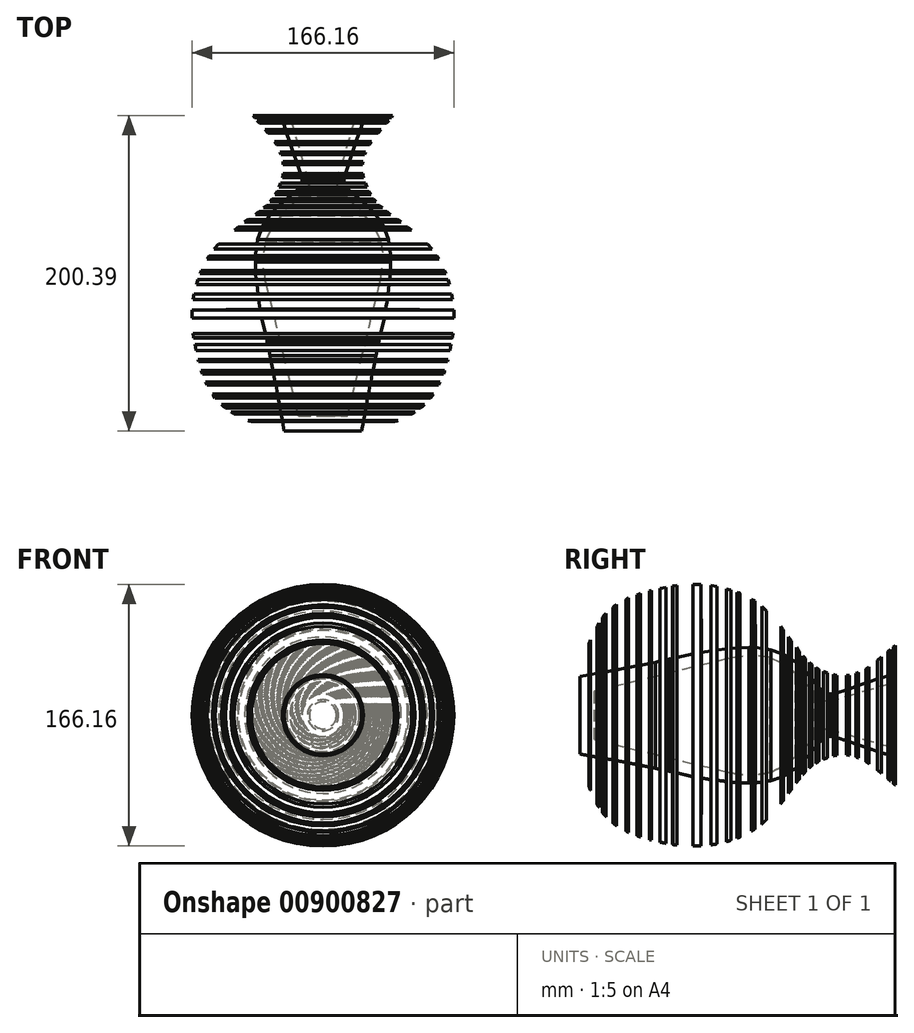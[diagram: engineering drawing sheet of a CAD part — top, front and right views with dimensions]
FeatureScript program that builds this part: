
annotation { "Feature Type Name" : "Feature", "Feature Type Description" : "" }
export const myFeature = defineFeature(function(context is Context, id is Id, definition is map)
    precondition{}
    {
        {
            var Q0;
            Q0=qCreatedBy(makeId("Top.planeOp"),FACE);
            var sketch = newSketch(context, id + "F0", { "sketchPlane" : qUnion([Q0])});
            skLineSegment(sketch, "E0", {"start": v(0, 0) * mm, "end": v(24.6, 0) * mm});
            skLineSegment(sketch, "E1", {"start": v(24.6, 0) * mm, "end": v(25.7, 6) * mm});
            skLineSegment(sketch, "E2", {"start": v(25.7, 6) * mm, "end": v(45.48, 6) * mm});
            skLineSegment(sketch, "E3", {"start": v(45.48, 6) * mm, "end": v(46.94, 6.45) * mm});
            skLineSegment(sketch, "E4", {"start": v(46.94, 6.45) * mm, "end": v(47.72, 6.74) * mm});
            skLineSegment(sketch, "E5", {"start": v(47.72, 6.74) * mm, "end": v(25.83, 6.74) * mm});
            skLineSegment(sketch, "E6", {"start": v(25.83, 6.74) * mm, "end": v(26.57, 10.86) * mm});
            skLineSegment(sketch, "E7", {"start": v(26.57, 10.86) * mm, "end": v(56.36, 10.86) * mm});
            skLineSegment(sketch, "E8", {"start": v(56.36, 10.86) * mm, "end": v(57.49, 11.54) * mm});
            skLineSegment(sketch, "E9", {"start": v(57.49, 11.54) * mm, "end": v(58.5, 12.14) * mm});
            skLineSegment(sketch, "E10", {"start": v(58.5, 12.14) * mm, "end": v(26.8, 12.14) * mm});
            skLineSegment(sketch, "E11", {"start": v(26.8, 12.14) * mm, "end": v(27.05, 13.55) * mm});
            skLineSegment(sketch, "E12", {"start": v(27.05, 13.55) * mm, "end": v(27.23, 14.54) * mm});
            skLineSegment(sketch, "E13", {"start": v(27.23, 14.54) * mm, "end": v(62, 14.54) * mm});
            skLineSegment(sketch, "E14", {"start": v(62, 14.54) * mm, "end": v(63.25, 15.43) * mm});
            skLineSegment(sketch, "E15", {"start": v(63.25, 15.43) * mm, "end": v(64.53, 16.71) * mm});
            skLineSegment(sketch, "E16", {"start": v(64.53, 16.71) * mm, "end": v(27.63, 16.71) * mm});
            skLineSegment(sketch, "E17", {"start": v(27.63, 16.71) * mm, "end": v(28.63, 22.26) * mm});
            skLineSegment(sketch, "E18", {"start": v(28.63, 22.26) * mm, "end": v(28.4, 20.96) * mm});
            skLineSegment(sketch, "E19", {"start": v(28.4, 20.96) * mm, "end": v(68.43, 20.96) * mm});
            skLineSegment(sketch, "E20", {"start": v(68.43, 20.96) * mm, "end": v(69.66, 22.52) * mm});
            skLineSegment(sketch, "E21", {"start": v(69.66, 22.52) * mm, "end": v(70.23, 23.46) * mm});
            skLineSegment(sketch, "E22", {"start": v(70.23, 23.46) * mm, "end": v(28.86, 23.46) * mm});
            skLineSegment(sketch, "E23", {"start": v(28.86, 23.46) * mm, "end": v(29.9, 29.26) * mm});
            skLineSegment(sketch, "E24", {"start": v(29.9, 29.26) * mm, "end": v(73.52, 29.26) * mm});
            skLineSegment(sketch, "E25", {"start": v(73.52, 29.26) * mm, "end": v(74.1, 30.42) * mm});
            skLineSegment(sketch, "E26", {"start": v(74.1, 30.42) * mm, "end": v(74.42, 31.1) * mm});
            skLineSegment(sketch, "E27", {"start": v(74.42, 31.1) * mm, "end": v(30.36, 31.1) * mm});
            skLineSegment(sketch, "E28", {"start": v(30.36, 31.1) * mm, "end": v(31.3, 36.27) * mm});
            skLineSegment(sketch, "E29", {"start": v(31.3, 36.27) * mm, "end": v(76.49, 36.27) * mm});
            skLineSegment(sketch, "E30", {"start": v(76.49, 36.27) * mm, "end": v(77.12, 37.9) * mm});
            skLineSegment(sketch, "E31", {"start": v(77.12, 37.9) * mm, "end": v(77.3, 38.46) * mm});
            skLineSegment(sketch, "E32", {"start": v(77.3, 38.46) * mm, "end": v(31.7, 38.46) * mm});
            skLineSegment(sketch, "E33", {"start": v(31.7, 38.46) * mm, "end": v(32.95, 44.17) * mm});
            skLineSegment(sketch, "E34", {"start": v(32.95, 44.17) * mm, "end": v(78.98, 44.17) * mm});
            skLineSegment(sketch, "E35", {"start": v(78.98, 44.17) * mm, "end": v(79.27, 45.4) * mm});
            skLineSegment(sketch, "E36", {"start": v(79.27, 45.4) * mm, "end": v(33.2, 45.4) * mm});
            skLineSegment(sketch, "E37", {"start": v(33.2, 45.4) * mm, "end": v(33.66, 47.97) * mm});
            skLineSegment(sketch, "E38", {"start": v(33.66, 47.97) * mm, "end": v(34.36, 51.04) * mm});
            skLineSegment(sketch, "E39", {"start": v(34.36, 51.04) * mm, "end": v(80.64, 51.04) * mm});
            skLineSegment(sketch, "E40", {"start": v(80.64, 51.04) * mm, "end": v(80.95, 52.75) * mm});
            skLineSegment(sketch, "E41", {"start": v(80.95, 52.75) * mm, "end": v(81.31, 54.77) * mm});
            skLineSegment(sketch, "E42", {"start": v(81.31, 54.77) * mm, "end": v(35.07, 54.77) * mm});
            skLineSegment(sketch, "E43", {"start": v(35.07, 54.77) * mm, "end": v(35.62, 57.06) * mm});
            skLineSegment(sketch, "E44", {"start": v(35.62, 57.06) * mm, "end": v(35.96, 58.91) * mm});
            skLineSegment(sketch, "E45", {"start": v(35.96, 58.91) * mm, "end": v(82.09, 58.91) * mm});
            skLineSegment(sketch, "E46", {"start": v(82.09, 58.91) * mm, "end": v(82.16, 59.32) * mm});
            skLineSegment(sketch, "E47", {"start": v(82.16, 59.32) * mm, "end": v(82.36, 61.16) * mm});
            skLineSegment(sketch, "E48", {"start": v(82.36, 61.16) * mm, "end": v(82.43, 61.89) * mm});
            skLineSegment(sketch, "E49", {"start": v(82.43, 61.89) * mm, "end": v(36.61, 61.89) * mm});
            skLineSegment(sketch, "E50", {"start": v(36.61, 61.89) * mm, "end": v(39.04, 71.84) * mm});
            skLineSegment(sketch, "E51", {"start": v(39.04, 71.84) * mm, "end": v(83.08, 71.84) * mm});
            skLineSegment(sketch, "E52", {"start": v(83.08, 71.84) * mm, "end": v(83.08, 75.52) * mm});
            skLineSegment(sketch, "E53", {"start": v(83.08, 75.52) * mm, "end": v(83.08, 76.93) * mm});
            skLineSegment(sketch, "E54", {"start": v(83.08, 76.93) * mm, "end": v(39.87, 77.42) * mm});
            skLineSegment(sketch, "E55", {"start": v(39.87, 77.42) * mm, "end": v(40.95, 83.38) * mm});
            skLineSegment(sketch, "E56", {"start": v(40.95, 83.38) * mm, "end": v(82.36, 83.38) * mm});
            skLineSegment(sketch, "E57", {"start": v(82.36, 83.38) * mm, "end": v(81.76, 87.09) * mm});
            skLineSegment(sketch, "E58", {"start": v(81.76, 87.09) * mm, "end": v(41.38, 87.09) * mm});
            skLineSegment(sketch, "E59", {"start": v(41.38, 87.09) * mm, "end": v(41.75, 90.57) * mm});
            skLineSegment(sketch, "E60", {"start": v(41.75, 90.57) * mm, "end": v(42, 93.01) * mm});
            skLineSegment(sketch, "E61", {"start": v(42, 93.01) * mm, "end": v(80.64, 93.01) * mm});
            skLineSegment(sketch, "E62", {"start": v(80.64, 93.01) * mm, "end": v(80.36, 93.01) * mm});
            skLineSegment(sketch, "E63", {"start": v(80.36, 93.01) * mm, "end": v(79.73, 95.25) * mm});
            skLineSegment(sketch, "E64", {"start": v(79.73, 95.25) * mm, "end": v(79.5, 96.03) * mm});
            skLineSegment(sketch, "E65", {"start": v(79.5, 96.03) * mm, "end": v(42.38, 96.03) * mm});
            skLineSegment(sketch, "E66", {"start": v(42.38, 96.03) * mm, "end": v(42.54, 97.6) * mm});
            skLineSegment(sketch, "E67", {"start": v(42.54, 97.6) * mm, "end": v(42.8, 99.97) * mm});
            skLineSegment(sketch, "E68", {"start": v(42.8, 99.97) * mm, "end": v(78.06, 99.97) * mm});
            skLineSegment(sketch, "E69", {"start": v(78.06, 99.97) * mm, "end": v(77.56, 101.36) * mm});
            skLineSegment(sketch, "E70", {"start": v(77.56, 101.36) * mm, "end": v(77.3, 101.89) * mm});
            skLineSegment(sketch, "E71", {"start": v(77.3, 101.89) * mm, "end": v(42.86, 101.89) * mm});
            skLineSegment(sketch, "E72", {"start": v(42.86, 101.89) * mm, "end": v(42.92, 107.4) * mm});
            skLineSegment(sketch, "E73", {"start": v(42.92, 107.4) * mm, "end": v(42.92, 109.5) * mm});
            skLineSegment(sketch, "E74", {"start": v(42.92, 109.5) * mm, "end": v(73.57, 109.15) * mm});
            skLineSegment(sketch, "E75", {"start": v(73.57, 109.15) * mm, "end": v(72.46, 111.1) * mm});
            skLineSegment(sketch, "E76", {"start": v(72.46, 111.1) * mm, "end": v(42.92, 111.44) * mm});
            skLineSegment(sketch, "E77", {"start": v(42.92, 111.44) * mm, "end": v(42.52, 115.57) * mm});
            skLineSegment(sketch, "E78", {"start": v(42.52, 115.57) * mm, "end": v(69.25, 115.57) * mm});
            skLineSegment(sketch, "E79", {"start": v(69.25, 115.57) * mm, "end": v(66.24, 118.6) * mm});
            skLineSegment(sketch, "E80", {"start": v(66.24, 118.6) * mm, "end": v(42, 118.6) * mm});
            skLineSegment(sketch, "E81", {"start": v(42, 118.6) * mm, "end": v(41.52, 121.6) * mm});
            skLineSegment(sketch, "E82", {"start": v(41.52, 121.6) * mm, "end": v(39.4, 127.68) * mm});
            skLineSegment(sketch, "E83", {"start": v(39.4, 127.68) * mm, "end": v(56.25, 127.68) * mm});
            skLineSegment(sketch, "E84", {"start": v(56.25, 127.68) * mm, "end": v(54.55, 129) * mm});
            skLineSegment(sketch, "E85", {"start": v(54.55, 129) * mm, "end": v(53.8, 129.53) * mm});
            skLineSegment(sketch, "E86", {"start": v(53.8, 129.53) * mm, "end": v(38.6, 129.53) * mm});
            skLineSegment(sketch, "E87", {"start": v(38.6, 129.53) * mm, "end": v(37.71, 131.3) * mm});
            skLineSegment(sketch, "E88", {"start": v(37.71, 131.3) * mm, "end": v(36.95, 132.57) * mm});
            skLineSegment(sketch, "E89", {"start": v(36.95, 132.57) * mm, "end": v(49.7, 132.57) * mm});
            skLineSegment(sketch, "E90", {"start": v(49.7, 132.57) * mm, "end": v(47.16, 134.4) * mm});
            skLineSegment(sketch, "E91", {"start": v(47.16, 134.4) * mm, "end": v(35.76, 134.4) * mm});
            skLineSegment(sketch, "E92", {"start": v(35.76, 134.4) * mm, "end": v(33.2, 137.54) * mm});
            skLineSegment(sketch, "E93", {"start": v(33.2, 137.54) * mm, "end": v(42.92, 137.54) * mm});
            skLineSegment(sketch, "E94", {"start": v(42.92, 137.54) * mm, "end": v(41.45, 138.6) * mm});
            skLineSegment(sketch, "E95", {"start": v(41.45, 138.6) * mm, "end": v(40.57, 139.4) * mm});
            skLineSegment(sketch, "E96", {"start": v(40.57, 139.4) * mm, "end": v(31.7, 139.4) * mm});
            skLineSegment(sketch, "E97", {"start": v(31.7, 139.4) * mm, "end": v(29.27, 141.92) * mm});
            skLineSegment(sketch, "E98", {"start": v(29.27, 141.92) * mm, "end": v(37.71, 141.82) * mm});
            skLineSegment(sketch, "E99", {"start": v(37.71, 141.82) * mm, "end": v(35.99, 143.24) * mm});
            skLineSegment(sketch, "E100", {"start": v(35.99, 143.24) * mm, "end": v(27.84, 143.24) * mm});
            skLineSegment(sketch, "E101", {"start": v(27.84, 143.24) * mm, "end": v(25.09, 145.76) * mm});
            skLineSegment(sketch, "E102", {"start": v(25.09, 145.76) * mm, "end": v(33.58, 145.76) * mm});
            skLineSegment(sketch, "E103", {"start": v(33.58, 145.76) * mm, "end": v(32.2, 147.37) * mm});
            skLineSegment(sketch, "E104", {"start": v(32.2, 147.37) * mm, "end": v(22.95, 147.48) * mm});
            skLineSegment(sketch, "E105", {"start": v(22.95, 147.48) * mm, "end": v(19.9, 150.05) * mm});
            skLineSegment(sketch, "E106", {"start": v(19.9, 150.05) * mm, "end": v(30.44, 150.05) * mm});
            skLineSegment(sketch, "E107", {"start": v(30.44, 150.05) * mm, "end": v(29.23, 152.04) * mm});
            skLineSegment(sketch, "E108", {"start": v(29.23, 152.04) * mm, "end": v(17.54, 152.04) * mm});
            skLineSegment(sketch, "E109", {"start": v(17.54, 152.04) * mm, "end": v(15.8, 153.87) * mm});
            skLineSegment(sketch, "E110", {"start": v(15.8, 153.87) * mm, "end": v(15.02, 154.8) * mm});
            skLineSegment(sketch, "E111", {"start": v(15.02, 154.8) * mm, "end": v(27.91, 154.8) * mm});
            skLineSegment(sketch, "E112", {"start": v(27.91, 154.8) * mm, "end": v(26.91, 157.44) * mm});
            skLineSegment(sketch, "E113", {"start": v(26.91, 157.44) * mm, "end": v(13.65, 157.44) * mm});
            skLineSegment(sketch, "E114", {"start": v(13.65, 157.44) * mm, "end": v(13.4, 157.86) * mm});
            skLineSegment(sketch, "E115", {"start": v(13.4, 157.86) * mm, "end": v(13.4, 159.06) * mm});
            skLineSegment(sketch, "E116", {"start": v(13.4, 159.06) * mm, "end": v(13.65, 161.03) * mm});
            skLineSegment(sketch, "E117", {"start": v(13.65, 161.03) * mm, "end": v(25.8, 161.03) * mm});
            skLineSegment(sketch, "E118", {"start": v(25.8, 161.03) * mm, "end": v(25.43, 162.85) * mm});
            skLineSegment(sketch, "E119", {"start": v(25.43, 162.85) * mm, "end": v(25.43, 163.38) * mm});
            skLineSegment(sketch, "E120", {"start": v(25.43, 163.38) * mm, "end": v(14.17, 163.38) * mm});
            skLineSegment(sketch, "E121", {"start": v(14.17, 163.38) * mm, "end": v(16.22, 169.3) * mm});
            skLineSegment(sketch, "E122", {"start": v(16.22, 169.3) * mm, "end": v(25.23, 169.3) * mm});
            skLineSegment(sketch, "E123", {"start": v(25.23, 169.3) * mm, "end": v(25.23, 170.07) * mm});
            skLineSegment(sketch, "E124", {"start": v(25.23, 170.07) * mm, "end": v(25.38, 171.23) * mm});
            skLineSegment(sketch, "E125", {"start": v(25.38, 171.23) * mm, "end": v(16.85, 171.23) * mm});
            skLineSegment(sketch, "E126", {"start": v(16.85, 171.23) * mm, "end": v(18.25, 175.4) * mm});
            skLineSegment(sketch, "E127", {"start": v(18.25, 175.4) * mm, "end": v(26.48, 175.4) * mm});
            skLineSegment(sketch, "E128", {"start": v(26.48, 175.4) * mm, "end": v(27.11, 177.13) * mm});
            skLineSegment(sketch, "E129", {"start": v(27.11, 177.13) * mm, "end": v(18.85, 177.13) * mm});
            skLineSegment(sketch, "E130", {"start": v(18.85, 177.13) * mm, "end": v(20.47, 181.82) * mm});
            skLineSegment(sketch, "E131", {"start": v(20.47, 181.82) * mm, "end": v(29.45, 181.82) * mm});
            skLineSegment(sketch, "E132", {"start": v(29.45, 181.82) * mm, "end": v(30.8, 183.67) * mm});
            skLineSegment(sketch, "E133", {"start": v(30.8, 183.67) * mm, "end": v(21.11, 183.67) * mm});
            skLineSegment(sketch, "E134", {"start": v(21.11, 183.67) * mm, "end": v(23, 189.16) * mm});
            skLineSegment(sketch, "E135", {"start": v(23, 189.16) * mm, "end": v(34.94, 189.16) * mm});
            skLineSegment(sketch, "E136", {"start": v(34.94, 189.16) * mm, "end": v(36.93, 191.58) * mm});
            skLineSegment(sketch, "E137", {"start": v(36.93, 191.58) * mm, "end": v(23.82, 191.58) * mm});
            skLineSegment(sketch, "E138", {"start": v(23.82, 191.58) * mm, "end": v(25.06, 195.69) * mm});
            skLineSegment(sketch, "E139", {"start": v(25.06, 195.69) * mm, "end": v(40.37, 195.69) * mm});
            skLineSegment(sketch, "E140", {"start": v(40.37, 195.69) * mm, "end": v(41.8, 197.18) * mm});
            skLineSegment(sketch, "E141", {"start": v(41.8, 197.18) * mm, "end": v(25.8, 197.18) * mm});
            skLineSegment(sketch, "E142", {"start": v(25.8, 197.18) * mm, "end": v(26.48, 199.1) * mm});
            skLineSegment(sketch, "E143", {"start": v(26.48, 199.1) * mm, "end": v(43.37, 199.1) * mm});
            skLineSegment(sketch, "E144", {"start": v(43.37, 199.1) * mm, "end": v(44.3, 200.39) * mm});
            skLineSegment(sketch, "E145", {"start": v(44.3, 200.39) * mm, "end": v(23.99, 200.03) * mm});
            skLineSegment(sketch, "E146", {"start": v(23.99, 200.03) * mm, "end": v(20.87, 200.03) * mm});
            skLineSegment(sketch, "E147", {"start": v(20.87, 200.03) * mm, "end": v(8.6, 157.44) * mm});
            skLineSegment(sketch, "E148", {"start": v(8.6, 157.44) * mm, "end": v(9.9, 153.61) * mm});
            skLineSegment(sketch, "E149", {"start": v(9.9, 153.61) * mm, "end": v(15.12, 148.65) * mm});
            skLineSegment(sketch, "E150", {"start": v(15.12, 148.65) * mm, "end": v(26.48, 136.87) * mm});
            skLineSegment(sketch, "E151", {"start": v(26.48, 136.87) * mm, "end": v(33.2, 127.72) * mm});
            skLineSegment(sketch, "E152", {"start": v(33.2, 127.72) * mm, "end": v(36.61, 120.74) * mm});
            skLineSegment(sketch, "E153", {"start": v(36.61, 120.74) * mm, "end": v(38.4, 109.22) * mm});
            skLineSegment(sketch, "E154", {"start": v(38.4, 109.22) * mm, "end": v(36.61, 96.08) * mm});
            skLineSegment(sketch, "E155", {"start": v(36.61, 96.08) * mm, "end": v(32.98, 81.16) * mm});
            skLineSegment(sketch, "E156", {"start": v(32.98, 81.16) * mm, "end": v(19.9, 27.5) * mm});
            skLineSegment(sketch, "E157", {"start": v(19.9, 27.5) * mm, "end": v(15.49, 9.38) * mm});
            skLineSegment(sketch, "E158", {"start": v(15.49, 9.38) * mm, "end": v(0, 9.38) * mm});
            skLineSegment(sketch, "E159", {"start": v(0, 9.38) * mm, "end": v(0, 0) * mm});
            skLineSegment(sketch, "E160", {"start": v(0, 0) * mm, "end": v(0, 9.38) * mm});
            skSolve(sketch);
        }
        {
            var Q0;
            Q0=qCreatedBy(makeId("Top.planeOp"),FACE);
            var sketch = newSketch(context, id + "F1", { "sketchPlane" : qUnion([Q0])});
            skLineSegment(sketch, "E161", {"start": v(0, 0) * mm, "end": v(0, 202.74) * mm});
            skSolve(sketch);
        }
        {
            var Q0;
            Q0 = qSketchRegion(id + "F0", true);
            var Q1;
            Q1=sQuery(id+"F1.wireOp",EDGE,"E161");
            revolve(context, id + "F2", {"surfaceOperationType" : NewSurfaceOperationType.NEW, "entities" : qUnion([Q0]), "axis" : qUnion([Q1]), "revolveType" : RevolveType.FULL});
        }
    });
